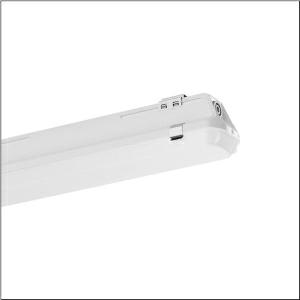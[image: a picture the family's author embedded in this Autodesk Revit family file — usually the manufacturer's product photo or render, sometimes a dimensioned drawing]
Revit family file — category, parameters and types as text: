
# Revit family: monsun_r__21_51fb107p480b_58b6
name_source: partatom
category: Lighting Fixtures
units: mm (PartAtom-declared; Revit-internal decimal feet)

## family parameters
Cut with Voids When Loaded = No
Host = Face
Light Source = No
Part Type = Normal
Room Calculation Point = No
Round Connector Dimension = Use Diameter
Shared = No

## types (1)
- Monsun® 21 (1 x LED, 8070 lm, 52.8 W, 4000K)
    Apparent Load = 53 VA
    CIE Flux Codes = 47 77 93 94 100
    Color Rendering = 80
    Color Temperature = 4000K
    Default Elevation = 1800 mm
    Description = Monsun® 21, damp-proof luminaire, chain hanger, primary optical cover: enclosure, of PMMA, light emission: direct distribution, primary light characteristic: symmetric, installation type: suspended mounting, surface-mounted, horizontal mounting, vertical mounting, LED, rated luminous flux: 8.070lm, luminous efficacy: 153lm/W, light colour: 840, colour temperature: 4000K, control gear: ECG, with terminal, 3-pole, max. 2.5mm², mains connection: 220..240V, AC, 50/60Hz, rated input power: 53W, housing, of glass-fibre reinforced polyester, uncoated, bright grey, incl. chain hanger, length: 1.590mm, width: 90mm, height: 88mm, clip for enclosure, of stainless steel (V2A), ceiling mounting element, of stainless steel (V2A), chain hanger, of stainless steel (V2A), protection rating (complete): IP66, insulation class (complete): insulation class I (protective earthing), certification: CE, ENEC, VDE, UKCA, protection symbol: D, impact resistance: IK04, permissible operating ambient temperature: -25..+35°C, standard: EN 50419, EN 60598-2-1, corresponds to IFS (International Featured Standards) requirements for safety and quality in the food industry, for indoor or canopied outdoor use, no direct snow, no direct sun, no direct rain, contact your sales advisor before using the luminaires in applications with unclear chemical exposure, large temperature fluctuations or condensation-forming humidity, LABS conformity tested according to VDMA 24364:2018-05, packaging unit: 1 piece
    Height = 89 mm
    Lamp = 1 x LED
    Lamp Light Flux = 8070 lm
    Lamp Power = 52.8 W
    Lamp count = 1
    Length = 1590 mm
    Luminous efficacy = 153 lm/W
    Manufacturer = Siteco
    ModVariant = No
    Model = 51FB107P480B
    Mounting Place = Ceiling
    Mounting Type = Surface mounted
    Number of Poles = 1
    OnlyDefault = Yes
    Power Factor = 1
    Product Name = Monsun® 21
    Product group = damp-proof luminaire
    ProductGroupID = 300
    Protection Class = Protection class I
    Protection Degree = IP 66
    RLX_Detail_Level = 1
    RLX_Emergency_Light_Flux = 0 lm
    RLX_Emergency_Type = 0
    RLX_Emergency_Type_DB = No
    RlxData = <blob elided: 88585 chars, md5=d3825d5e>
    Socket = socket
    Standby Power = 0 W
    System Light Flux = 8070 lm
    System Power = 53 W
    Type Comments = Product without accessories
    Type Image = l_1319656.jpg
    URL = http://relux.com
    VarID = ---
    Voltage = 0 V
    Weight = 0.00 kg
    Width = 90 mm

## geometry (parser evidence)
native form markers: Blend x4, Sweep x14
no freeform markers — native parametric forms only
